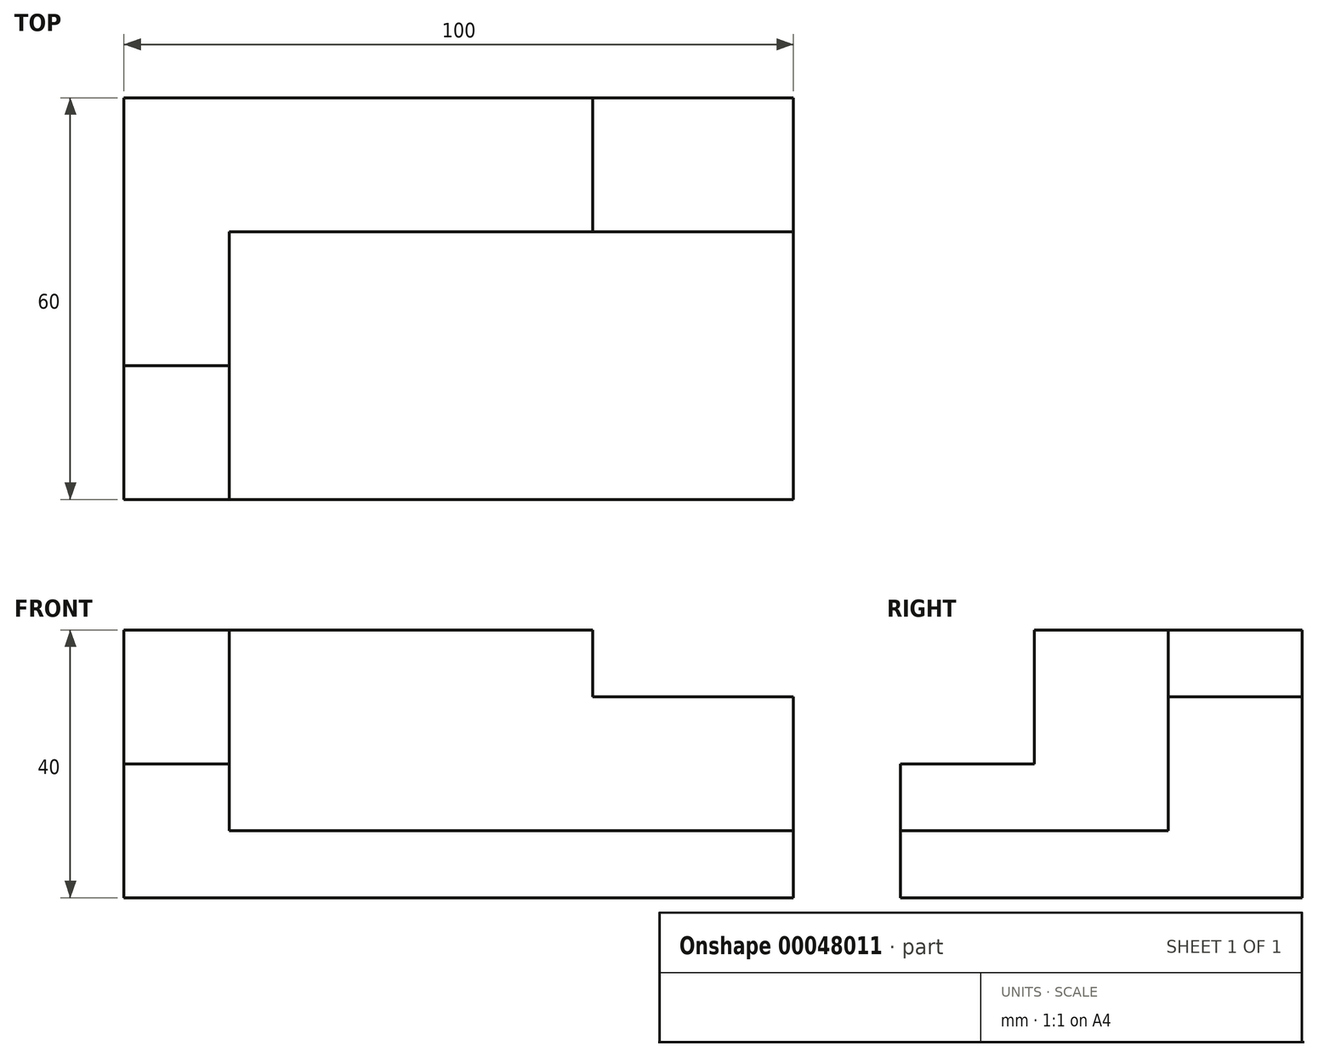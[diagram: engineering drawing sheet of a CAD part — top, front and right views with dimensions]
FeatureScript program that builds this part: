
annotation { "Feature Type Name" : "Feature", "Feature Type Description" : "" }
export const myFeature = defineFeature(function(context is Context, id is Id, definition is map)
    precondition{}
    {
        {
            var Q0;
            Q0=qCreatedBy(makeId("Front.planeOp"),FACE);
            var sketch = newSketch(context, id + "F0", { "sketchPlane" : qUnion([Q0])});
            skLineSegment(sketch, "E0", {"start": v(0, 0) * mm, "end": v(0, 40) * mm});
            skLineSegment(sketch, "E1", {"start": v(0, 40) * mm, "end": v(70, 40) * mm});
            skLineSegment(sketch, "E2", {"start": v(70, 40) * mm, "end": v(70, 30) * mm});
            skLineSegment(sketch, "E3", {"start": v(70, 30) * mm, "end": v(100, 30) * mm});
            skLineSegment(sketch, "E4", {"start": v(100, 30) * mm, "end": v(100, 0) * mm});
            skLineSegment(sketch, "E5", {"start": v(100, 0) * mm, "end": v(0, 0) * mm});
            skLineSegment(sketch, "E6", {"start": v(100, 10) * mm, "end": v(15.7, 10) * mm});
            skLineSegment(sketch, "E7", {"start": v(15.7, 10) * mm, "end": v(15.7, 40) * mm});
            skLineSegment(sketch, "E8", {"start": v(15.7, 20) * mm, "end": v(0, 20) * mm});
            skSolve(sketch);
        }
        {
            var Q0;
            Q0 = qSketchRegion(id + "F0", true);
            extrude(context, id + "F1", {"entities" : qUnion([Q0]), "oppositeDirection" : true, "depth" : 60 * mm});
        }
        {
            var Q0;
            {var subQ5=sQuery(id+"F0.wireOp",EDGE,"E2");Q0=makeQuery(id+"F0.imprint","IMPRINT",FACE,{"disambiguationData":[TD([[makeQuery(id+"F0.imprint","IMPRINT",EDGE,{"derivedFrom":subQ5}),-1.0]])]});}
            extrude(context, id + "F2", {"entities" : qUnion([Q0]), "operationType" : NewBodyOperationType.REMOVE, "oppositeDirection" : true, "depth" : 40 * mm});
        }
        {
            var Q0;
            {var subQ0=sQuery(id+"F0.wireOp",EDGE,"E8");Q0=makeQuery(id+"F0.imprint","IMPRINT",FACE,{"disambiguationData":[TD([[makeQuery(id+"F0.imprint","IMPRINT",EDGE,{"derivedFrom":subQ0}),-1.0]])]});}
            extrude(context, id + "F3", {"entities" : qUnion([Q0]), "operationType" : NewBodyOperationType.REMOVE, "oppositeDirection" : true, "depth" : 20 * mm});
        }
    });
